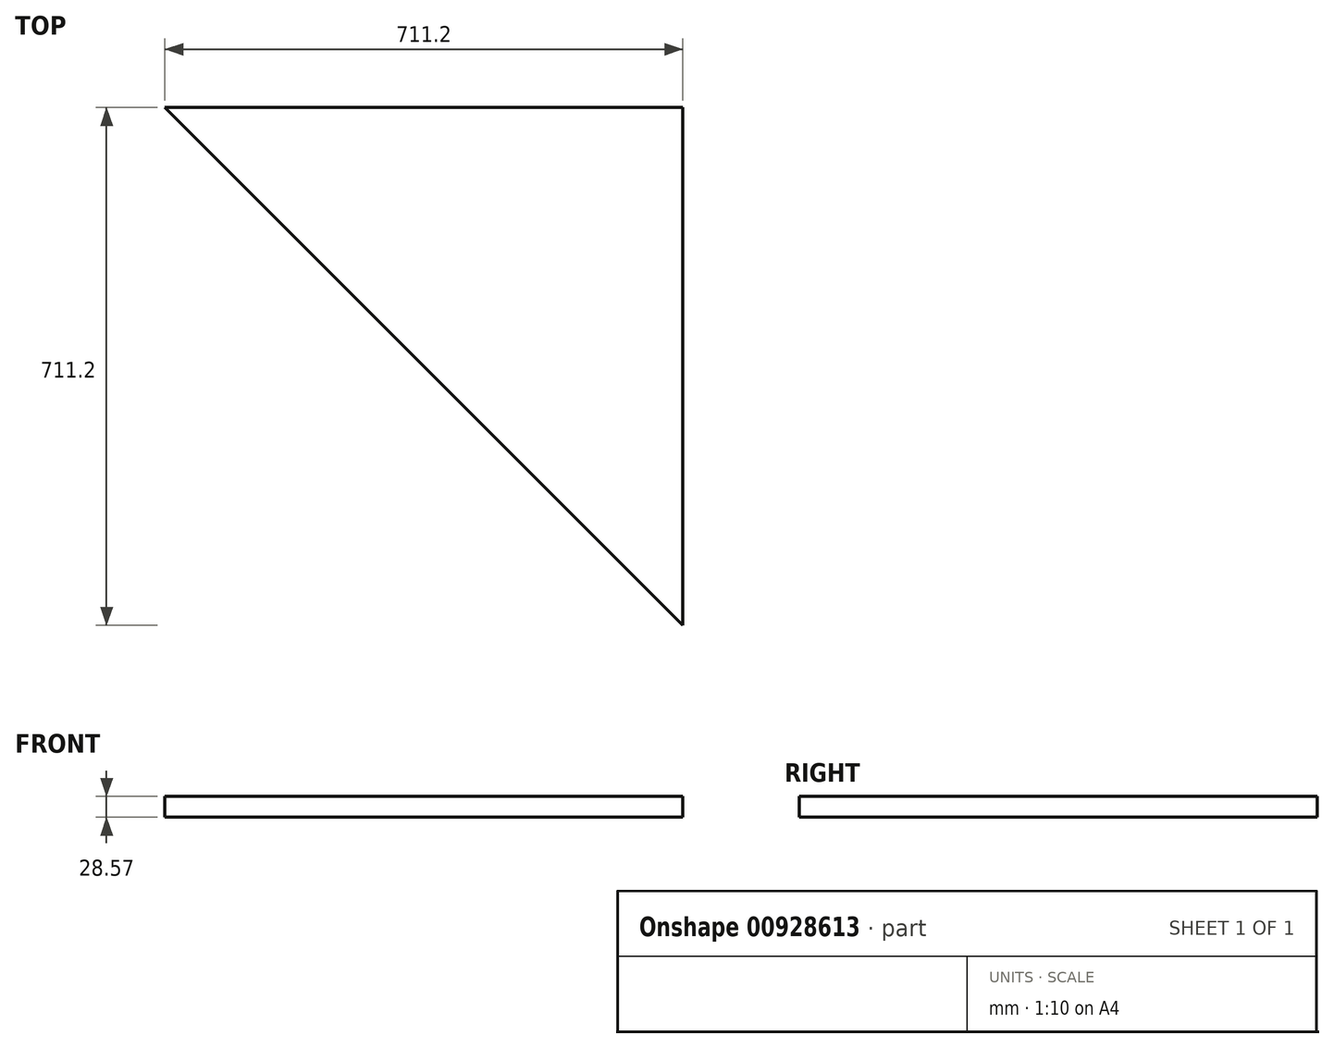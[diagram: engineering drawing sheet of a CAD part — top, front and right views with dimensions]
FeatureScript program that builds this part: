
annotation { "Feature Type Name" : "Feature", "Feature Type Description" : "" }
export const myFeature = defineFeature(function(context is Context, id is Id, definition is map)
    precondition{}
    {
        {
            var Q0;
            Q0=qCreatedBy(makeId("Top.planeOp"),FACE);
            var sketch = newSketch(context, id + "F0", { "sketchPlane" : qUnion([Q0])});
            skLineSegment(sketch, "E0.bottom", {"start": v(355.6, 355.6) * mm, "end": v(-355.6, 355.6) * mm});
            skLineSegment(sketch, "E0.top", {"start": v(355.6, -355.6) * mm, "end": v(-355.6, -355.6) * mm});
            skLineSegment(sketch, "E0.left", {"start": v(355.6, 355.6) * mm, "end": v(355.6, -355.6) * mm});
            skLineSegment(sketch, "E0.right", {"start": v(-355.6, 355.6) * mm, "end": v(-355.6, -355.6) * mm});
            skPoint(sketch, "E0.middle", {"position": v(0, 0) * mm});
            skLineSegment(sketch, "E1", {"start": v(-355.6, 355.6) * mm, "end": v(355.6, -355.6) * mm});
            skSolve(sketch);
        }
        {
            var Q0;
            Q0=makeQuery(id+"F0.imprint","IMPRINT",FACE,{"disambiguationData":[TD([[makeQuery(id+"F0.imprint","IMPRINT",EDGE,{"derivedFrom":sQuery(id+"F0.wireOp",EDGE,"E0.bottom")}),1.0]])]});
            extrude(context, id + "F1", {"entities" : qUnion([Q0]), "depth" : 28.57 * mm, "offsetDistance" : 25.4 * mm});
        }
    });
